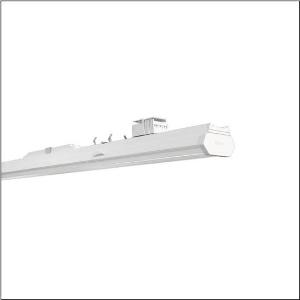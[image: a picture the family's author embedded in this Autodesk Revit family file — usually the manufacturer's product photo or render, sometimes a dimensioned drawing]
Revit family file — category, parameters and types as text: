
# Revit family: licross_r__21_protected_mo_52td11dn48xg_0db0
name_source: partatom
category: Lighting Fixtures
units: mm (PartAtom-declared; Revit-internal decimal feet)

## family parameters
Cut with Voids When Loaded = No
Host = Face
Light Source = No
Part Type = Normal
Room Calculation Point = No
Round Connector Dimension = Use Diameter
Shared = No

## types (1)
- --- (1 x LED, 8000 lm, 45.5 W, 4000K)
    Apparent Load = 46 VA
    CIE Flux Codes = 83 94 98 100 100
    Color Rendering = 80
    Color Temperature = 4000K
    Default Elevation = 1800 mm
    Description = Licross® 21 Protected MO, luminaire insert, of sheet steel, galvanised, coil coated, white, length: 1.500mm, width: 90mm, height: 103mm, LED rated luminous flux: 8.000lm, light colour: 840, control gear: DALI 2, with plug, 5-pole, with phase selection, mains connection: 220..240V, AC, 50/60Hz, rated input power: 46W, halogen-free wiring, primary light control with lens, of plastic, primary optical cover: cover, of PMMA, light emission: direct distribution, primary light characteristic: symmetric, protection rating (complete): IP54, insulation class (complete): insulation class I (protective earthing), certification: CE, ENEC, VDE, UKCA, protection symbol: D if used in an environment with non-conductive dust loads with corresponding accessories, impact resistance: IK06, permissible ambient temperature for indoor applications: -25..+45°C, corresponds to IFS (International Featured Standards) requirements for safety and quality in the food industry, reducing of maximum allowable ambient temperature of 5°C with ceiling mounting, LABS conformity tested according to VDMA 24364:2018-05, packaging unit: 1 piece
    Height = 92 mm
    Lamp = 1 x LED
    Lamp Light Flux = 8000 lm
    Lamp Power = 45.5 W
    Lamp count = 1
    Length = 1500 mm
    Luminous efficacy = 176 lm/W
    Manufacturer = Siteco
    ModVariant = No
    Model = 52TD11DN48XG
    Mounting Place = Ceiling
    Mounting Type = Pendant
    Number of Poles = 1
    OnlyDefault = Yes
    Power Factor = 1
    Product Name = Licross® 21 Protected MO
    Product group = luminaire insert
    ProductGroupID = 901
    Protection Class = Protection class I
    Protection Degree = IP 54
    RLX_Detail_Level = 1
    RLX_Emergency_Light_Flux = 0 lm
    RLX_Emergency_Type = 0
    RLX_Emergency_Type_DB = No
    RlxData = <blob elided: 24173 chars, md5=121ab542>
    Socket = socket
    Standby Power = 0 W
    System Light Flux = 8000 lm
    System Power = 46 W
    Type Comments = factory setting: luminous flux: 100 % | dim-lin: 254 | 307 mA
    Type Image = l_1256148.jpg
    URL = http://relux.com
    VarID = @adj_059869
    Voltage = 0 V
    Weight = 0.00 kg
    Width = 88 mm

## geometry (parser evidence)
native form markers: Blend x4, Sweep x11
no freeform markers — native parametric forms only
